FCSTD DOCUMENT  (FreeCAD 1.0R39109 (Git))
Label: FANA
License: All rights reserved
LicenseURL: http://en.wikipedia.org/wiki/All_rights_reserved
objects: Sketcher::SketchObject×1, PartDesign::Body×1
note: 3 computed .brp shape members not serialized (recipe doc carries the construction recipe); baked Part::Feature solids carry a one-line shape summary decoded from their .brp

FEATURE [Sketcher::SketchObject] Sketch
  ArcFitTolerance = 1e-06
  AttachmentSupport = -> [XY_Plane]
  FullyConstrained = false
  MakeInternals = false
  MapMode = 5
  sketch-geometry (57):
    g0: LineSegment StartX=0 StartY=0 StartZ=0 EndX=340 EndY=0 EndZ=0
    g1: LineSegment [constr] StartX=340 StartY=0 StartZ=0 EndX=340 EndY=300 EndZ=0
    g2: LineSegment StartX=340 StartY=300 StartZ=0 EndX=0 EndY=300 EndZ=0
    g3: LineSegment [constr] StartX=0 StartY=300 StartZ=0 EndX=0 EndY=0 EndZ=0
    g4: Circle CenterX=110 CenterY=150 CenterZ=0 NormalX=0 NormalY=0 NormalZ=1 AngleXU=0 Radius=57.125
    g5: Circle CenterX=240 CenterY=150 CenterZ=0 NormalX=0 NormalY=0 NormalZ=1 AngleXU=0 Radius=57.125
    g6: Circle [constr] CenterX=9.48273 CenterY=250 CenterZ=0 NormalX=0 NormalY=0 NormalZ=1 AngleXU=0 Radius=2.5
    g7: Circle [constr] CenterX=330 CenterY=250 CenterZ=0 NormalX=0 NormalY=0 NormalZ=1 AngleXU=0 Radius=2.5
    g8: Circle [constr] CenterX=330 CenterY=50 CenterZ=0 NormalX=0 NormalY=0 NormalZ=1 AngleXU=0 Radius=2.5
    g9: Circle [constr] CenterX=167.5 CenterY=150 CenterZ=0 NormalX=0 NormalY=0 NormalZ=1 AngleXU=0 Radius=5
    g10: Circle [constr] CenterX=110 CenterY=150 CenterZ=0 NormalX=0 NormalY=0 NormalZ=1 AngleXU=0 Radius=57.125
    g11: Circle [constr] CenterX=110 CenterY=150 CenterZ=0 NormalX=0 NormalY=0 NormalZ=1 AngleXU=0 Radius=57.125
    g12: Circle [constr] CenterX=110 CenterY=150 CenterZ=0 NormalX=0 NormalY=0 NormalZ=1 AngleXU=0 Radius=65
    g13: Circle [constr] CenterX=110 CenterY=150 CenterZ=0 NormalX=0 NormalY=0 NormalZ=1 AngleXU=0 Radius=60
    g14: Circle [constr] CenterX=240 CenterY=150 CenterZ=0 NormalX=0 NormalY=0 NormalZ=1 AngleXU=0 Radius=60
    g15: Circle [constr] CenterX=167.5 CenterY=150 CenterZ=0 NormalX=0 NormalY=0 NormalZ=1 AngleXU=0 Radius=10.75
    g16: ArcOfCircle [constr] CenterX=9.5 CenterY=50 CenterZ=0 NormalX=0 NormalY=0 NormalZ=1 AngleXU=0 Radius=3 StartAngle=1.5708 EndAngle=4.71239
    g17: ArcOfCircle [constr] CenterX=24.5 CenterY=50 CenterZ=0 NormalX=0 NormalY=0 NormalZ=1 AngleXU=0 Radius=3 StartAngle=4.71239 EndAngle=7.85398
    g18: LineSegment [constr] StartX=9.5 StartY=53 StartZ=0 EndX=24.5 EndY=53 EndZ=0
    g19: LineSegment [constr] StartX=9.5 StartY=47 StartZ=0 EndX=24.5 EndY=47 EndZ=0
    g20: ArcOfCircle [constr] CenterX=9.48273 CenterY=250 CenterZ=0 NormalX=0 NormalY=0 NormalZ=1 AngleXU=0 Radius=3 StartAngle=1.5708 EndAngle=4.71239
    g21: ArcOfCircle [constr] CenterX=24.4827 CenterY=250 CenterZ=0 NormalX=0 NormalY=0 NormalZ=1 AngleXU=0 Radius=3 StartAngle=4.71239 EndAngle=7.85398
    g22: LineSegment [constr] StartX=9.48273 StartY=253 StartZ=0 EndX=24.4827 EndY=253 EndZ=0
    g23: LineSegment [constr] StartX=9.48273 StartY=247 StartZ=0 EndX=24.4827 EndY=247 EndZ=0
    g24: ArcOfCircle CenterX=-75 CenterY=40 CenterZ=0 NormalX=0 NormalY=0 NormalZ=1 AngleXU=0 Radius=3 StartAngle=4.71239 EndAngle=7.85398
    g25: ArcOfCircle CenterX=-105 CenterY=40 CenterZ=0 NormalX=0 NormalY=0 NormalZ=1 AngleXU=0 Radius=3 StartAngle=1.5708 EndAngle=4.71239
    g26: LineSegment StartX=-75 StartY=37 StartZ=0 EndX=-105 EndY=37 EndZ=0
    g27: LineSegment StartX=-75 StartY=43 StartZ=0 EndX=-105 EndY=43 EndZ=0
    g28: ArcOfCircle [constr] CenterX=315 CenterY=49.9561 CenterZ=0 NormalX=0 NormalY=0 NormalZ=1 AngleXU=0 Radius=3 StartAngle=1.5708 EndAngle=4.71239
    g29: ArcOfCircle [constr] CenterX=330 CenterY=49.9561 CenterZ=0 NormalX=0 NormalY=0 NormalZ=1 AngleXU=0 Radius=3 StartAngle=4.71239 EndAngle=7.85398
    g30: LineSegment [constr] StartX=315 StartY=52.9561 StartZ=0 EndX=330 EndY=52.9561 EndZ=0
    g31: LineSegment [constr] StartX=315 StartY=46.9561 StartZ=0 EndX=330 EndY=46.9561 EndZ=0
    g32: LineSegment StartX=340 StartY=300 StartZ=0 EndX=455 EndY=300 EndZ=0
    g33: LineSegment StartX=340 StartY=0 StartZ=0 EndX=455 EndY=0 EndZ=0
    g34: LineSegment StartX=455 StartY=0 StartZ=0 EndX=455 EndY=300 EndZ=0
    g35: LineSegment StartX=-115 StartY=300 StartZ=0 EndX=0 EndY=300 EndZ=0
    g36: LineSegment StartX=-115 StartY=300 StartZ=0 EndX=0 EndY=300 EndZ=0
    g37: LineSegment StartX=-115 StartY=0 StartZ=0 EndX=0 EndY=0 EndZ=0
    g38: LineSegment StartX=-115 StartY=300 StartZ=0 EndX=-115 EndY=0 EndZ=0
    g39: Circle [constr] CenterX=330 CenterY=250 CenterZ=0 NormalX=0 NormalY=0 NormalZ=1 AngleXU=0 Radius=2.5
    g40: ArcOfCircle [constr] CenterX=315 CenterY=249.998 CenterZ=0 NormalX=0 NormalY=0 NormalZ=1 AngleXU=0 Radius=3 StartAngle=1.5708 EndAngle=4.71239
    g41: ArcOfCircle [constr] CenterX=330 CenterY=249.998 CenterZ=0 NormalX=0 NormalY=0 NormalZ=1 AngleXU=0 Radius=3 StartAngle=4.71239 EndAngle=7.85398
    g42: LineSegment [constr] StartX=315 StartY=252.998 StartZ=0 EndX=330 EndY=252.998 EndZ=0
    g43: LineSegment [constr] StartX=315 StartY=246.998 StartZ=0 EndX=330 EndY=246.998 EndZ=0
    g44: ArcOfCircle CenterX=415 CenterY=260 CenterZ=0 NormalX=0 NormalY=0 NormalZ=1 AngleXU=0 Radius=3 StartAngle=1.5708 EndAngle=4.71239
    g45: ArcOfCircle CenterX=445 CenterY=260 CenterZ=0 NormalX=0 NormalY=0 NormalZ=1 AngleXU=0 Radius=3 StartAngle=4.71239 EndAngle=7.85398
    g46: LineSegment StartX=415 StartY=263 StartZ=0 EndX=445 EndY=263 EndZ=0
    g47: LineSegment StartX=415 StartY=257 StartZ=0 EndX=445 EndY=257 EndZ=0
    g48: ArcOfCircle CenterX=415 CenterY=40 CenterZ=0 NormalX=0 NormalY=0 NormalZ=1 AngleXU=0 Radius=3 StartAngle=1.5708 EndAngle=4.71239
    g49: ArcOfCircle CenterX=445 CenterY=40 CenterZ=0 NormalX=0 NormalY=0 NormalZ=1 AngleXU=0 Radius=3 StartAngle=4.71239 EndAngle=7.85398
    g50: LineSegment StartX=415 StartY=43 StartZ=0 EndX=445 EndY=43 EndZ=0
    g51: LineSegment StartX=415 StartY=37 StartZ=0 EndX=445 EndY=37 EndZ=0
    g52: ArcOfCircle CenterX=-105 CenterY=260 CenterZ=0 NormalX=0 NormalY=0 NormalZ=1 AngleXU=0 Radius=3 StartAngle=1.5708 EndAngle=4.71239
    g53: ArcOfCircle CenterX=-75 CenterY=260 CenterZ=0 NormalX=0 NormalY=0 NormalZ=1 AngleXU=0 Radius=3 StartAngle=4.71239 EndAngle=7.85398
    g54: LineSegment StartX=-105 StartY=263 StartZ=0 EndX=-75 EndY=263 EndZ=0
    g55: LineSegment StartX=-105 StartY=257 StartZ=0 EndX=-75 EndY=257 EndZ=0
    g56: LineSegment [constr] StartX=167.125 StartY=150 StartZ=0 EndX=182.875 EndY=150 EndZ=0
  constraints (139):
    c: Coincident(g0,g1)
    c: Coincident(g1,g2)
    c: Coincident(g2,g3)
    c: Coincident(g3,g0)
    c: Horizontal(g0)
    c: Horizontal(g2)
    c: Vertical(g1)
    c: Vertical(g3)
    c: Coincident(g0,g-1)
    c: DistanceX(g0,g0) = 340
    c: DistanceY(g3,g3) = 300
    c: Diameter(g4) = 114.25
    c: Diameter(g5) = 114.25
    c: DistanceY(g4,g2) = 150
    c: Horizontal(g4,g5)
    c: DistanceX(g-1,g4) = 110
    c: Distance(g5,g1) = 100
    c: Horizontal(g6,g7)
    c: DistanceX(g-1,g8) = 330
    c: Diameter(g6) = 5
    c: Diameter(g8) = 5
    c: Diameter(g7) = 5
    c: Diameter(g9) = 10
    c: DistanceX(g2,g9) = 167.5
    c: DistanceY(g0,g9) = 150
    c: DistanceY(g6,g2) = 50
    c: Coincident(g10,g4)
    c: Equal(g10,g4)
    c: Coincident(g11,g4)
    c: Equal(g11,g4)
    c: Diameter(g12) = 130
    c: Coincident(g12,g4)
    c: DistanceX(g8,g7) = 0
    c: Coincident(g13,g4)
    c: Diameter(g13) = 120
    c: Coincident(g14,g5)
    c: Diameter(g14) = 120
    c: Diameter(g15) = 21.5
    c: Coincident(g15,g9)
    c: Tangent(g16,g18) = 1.5708
    c: Tangent(g16,g19) = -1.5708
    c: Tangent(g17,g18) = 1.5708
    c: Tangent(g17,g19) = -1.5708
    c: Equal(g16,g17)
    c: Horizontal(g19)
    c: Distance(g16,g17) = 15
    c: Radius(g16) = 3
    c: DistanceY(g0,g16) = 47
    c: DistanceX(g0,g16) = 9.5
    c: Tangent(g20,g22) = 1.5708
    c: Tangent(g20,g23) = -1.5708
    c: Tangent(g21,g22) = 1.5708
    c: Tangent(g21,g23) = -1.5708
    c: Equal(g20,g21)
    c: Horizontal(g23)
    c: Distance(g20,g21) = 15
    c: Radius(g20) = 3
    c: Coincident(g20,g6)
    c: Tangent(g24,g26) = 1.5708
    c: Tangent(g24,g27) = -1.5708
    c: Tangent(g25,g26) = 1.5708
    c: Tangent(g25,g27) = -1.5708
    c: Equal(g24,g25)
    c: Horizontal(g27)
    c: Distance(g24,g25) = 30
    c: Radius(g24) = 3
    c: Tangent(g28,g30) = 1.5708
    c: Tangent(g28,g31) = -1.5708
    c: Tangent(g29,g30) = 1.5708
    c: Tangent(g29,g31) = -1.5708
    c: Equal(g28,g29)
    c: Horizontal(g31)
    c: Distance(g28,g29) = 15
    c: Radius(g28) = 3
    c: DistanceX(g8,g29) = 0
    c: Distance(g32) = 115
    c: Coincident(g32,g1)
    c: Horizontal(g32)
    c: Distance(g33) = 115
    c: Coincident(g33,g0)
    c: PointOnObject(g33,g-1)
    c: Coincident(g34,g33)
    c: Coincident(g34,g32)
    c: Distance(g35) = 115
    c: Horizontal(g36)
    c: Coincident(g36,g35)
    c: Coincident(g36,g35)
    c: Coincident(g35,g2)
    c: Distance(g37) = 115
    c: Horizontal(g37)
    c: Coincident(g37,g0)
    c: Coincident(g38,g35)
    c: Coincident(g38,g37)
    c: Diameter(g39) = 5
    c: Tangent(g40,g42) = 1.5708
    c: Tangent(g40,g43) = -1.5708
    c: Tangent(g41,g42) = 1.5708
    c: Tangent(g41,g43) = -1.5708
    c: Equal(g40,g41)
    c: Horizontal(g43)
    c: Distance(g40,g41) = 15
    c: Radius(g40) = 3
    c: DistanceX(g39,g41) = 0
    c: Tangent(g44,g46) = 1.5708
    c: Tangent(g44,g47) = -1.5708
    c: Tangent(g45,g46) = 1.5708
    c: Tangent(g45,g47) = -1.5708
    c: Equal(g44,g45)
    c: Horizontal(g47)
    c: Distance(g44,g45) = 30
    c: Radius(g44) = 3
    c: Tangent(g48,g50) = 1.5708
    c: Tangent(g48,g51) = -1.5708
    c: Tangent(g49,g50) = 1.5708
    c: Tangent(g49,g51) = -1.5708
    c: Equal(g48,g49)
    c: Horizontal(g51)
    c: Distance(g48,g49) = 30
    c: Radius(g48) = 3
    c: Tangent(g52,g54) = 1.5708
    c: Tangent(g52,g55) = -1.5708
    c: Tangent(g53,g54) = 1.5708
    c: Tangent(g53,g55) = -1.5708
    c: Equal(g52,g53)
    c: Horizontal(g55)
    c: Distance(g52,g53) = 30
    c: Radius(g52) = 3
    c: DistanceX(g49,g33) = 10
    c: DistanceY(g33,g49) = 40
    c: DistanceY(g45,g32) = 40
    c: DistanceX(g45,g32) = 10
    c: DistanceX(g35,g52) = 10
    c: DistanceY(g52,g35) = 40
    c: DistanceY(g37,g24) = 40
    c: DistanceX(g25,g37) = -10
    c: PointOnObject(g56,g4)
    c: PointOnObject(g56,g5)
    c: Horizontal(g56)
    c: DistanceX(g56,g56) = 15.75
FEATURE [PartDesign::Body] Body
  AllowCompound = false
  Group = -> [Sketch]
  Origin = -> Origin
